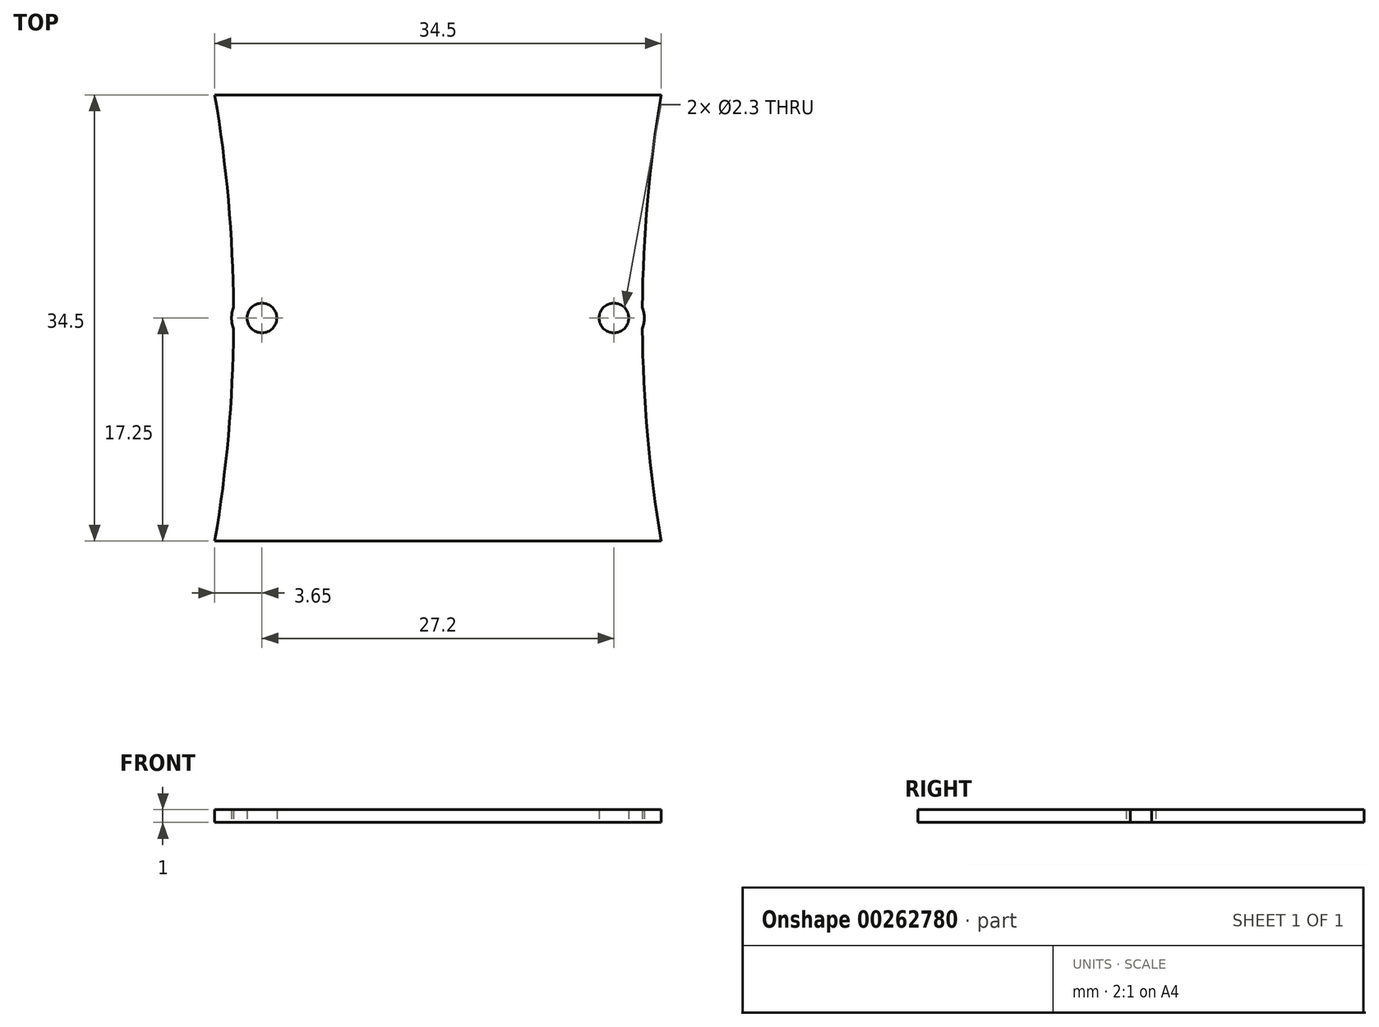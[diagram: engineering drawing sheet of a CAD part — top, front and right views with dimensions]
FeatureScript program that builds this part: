
annotation { "Feature Type Name" : "Feature", "Feature Type Description" : "" }
export const myFeature = defineFeature(function(context is Context, id is Id, definition is map)
    precondition{}
    {
        {
            var Q0;
            Q0=qCreatedBy(makeId("Top.planeOp"),FACE);
            var sketch = newSketch(context, id + "F0", { "sketchPlane" : qUnion([Q0])});
            skCircle(sketch, "E0", {"center": v(-13.6, 0) * mm, "radius": 1.15 * mm});
            skCircle(sketch, "E1.MirrorC", {"center": v(13.6, 0) * mm, "radius": 1.15 * mm});
            skArc(sketch, "E2", {"start": v(-15.8, 0.83) * mm, "mid": v(-15.95, 0) * mm, "end": v(-15.8, -0.83) * mm});
            skArc(sketch, "E3", {"start": v(-15.8, 0.83) * mm, "mid": v(-16.2, 9.07) * mm, "end": v(-17.25, 17.25) * mm});
            skArc(sketch, "E4.MirrorCS", {"start": v(15.8, 0.83) * mm, "mid": v(16.2, 9.07) * mm, "end": v(17.25, 17.25) * mm});
            skArc(sketch, "E5.MirrorCS", {"start": v(15.8, 0.83) * mm, "mid": v(15.95, 0) * mm, "end": v(15.8, -0.83) * mm});
            skLineSegment(sketch, "E6.bottom", {"start": v(-17.25, 17.25) * mm, "end": v(17.25, 17.25) * mm});
            skLineSegment(sketch, "E6.top", {"start": v(-17.25, -17.25) * mm, "end": v(17.25, -17.25) * mm});
            skArc(sketch, "E7.trimOffspring", {"start": v(-17.25, -17.25) * mm, "mid": v(-16.2, -9.07) * mm, "end": v(-15.8, -0.83) * mm});
            skArc(sketch, "E8.trimOffspring", {"start": v(17.25, -17.25) * mm, "mid": v(16.2, -9.07) * mm, "end": v(15.8, -0.83) * mm});
            skLineSegment(sketch, "E9", {"start": v(0, 17.25) * mm, "end": v(0, -17.25) * mm, "construction": true});
            skSolve(sketch);
        }
        {
            var Q0;
            Q0 = qSketchRegion(id + "F0", true);
            extrude(context, id + "F1", {"entities" : qUnion([Q0]), "depth" : 1 * mm});
        }
    });
